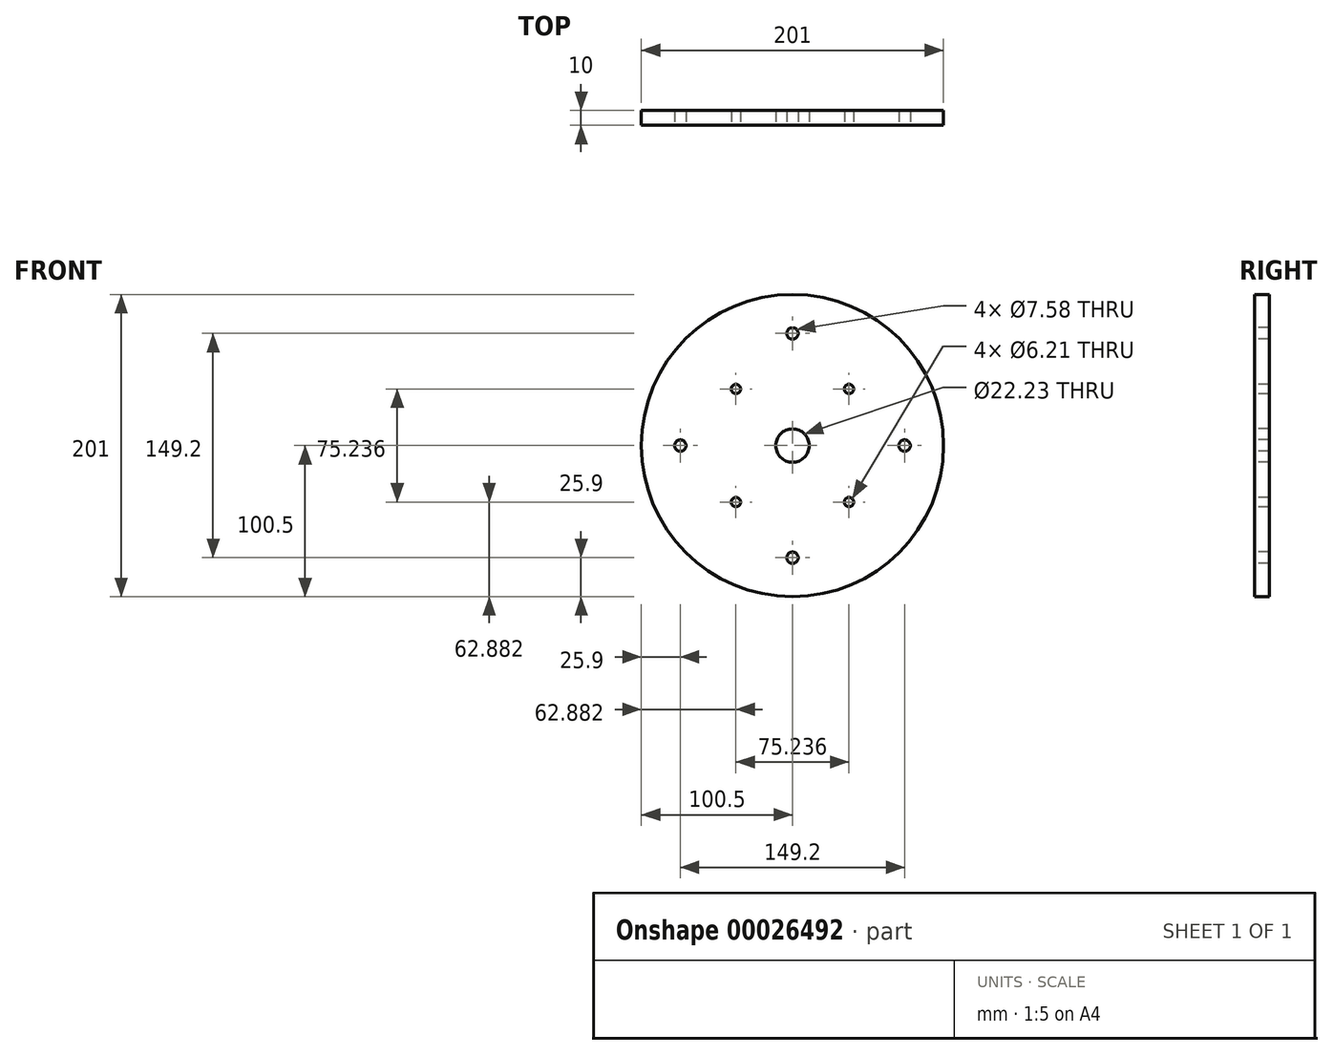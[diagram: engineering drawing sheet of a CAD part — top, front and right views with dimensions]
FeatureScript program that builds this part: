
annotation { "Feature Type Name" : "Feature", "Feature Type Description" : "" }
export const myFeature = defineFeature(function(context is Context, id is Id, definition is map)
    precondition{}
    {
        {
            var Q0;
            Q0=qCreatedBy(makeId("Front.planeOp"),FACE);
            var sketch = newSketch(context, id + "F0", { "sketchPlane" : qUnion([Q0])});
            skCircle(sketch, "E0", {"center": v(0, 0) * mm, "radius": 100.5 * mm});
            skCircle(sketch, "E1", {"center": v(0, 0) * mm, "radius": 53.2 * mm, "construction": true});
            skCircle(sketch, "E2", {"center": v(0, 0) * mm, "radius": 74.6 * mm, "construction": true});
            skLineSegment(sketch, "E3", {"start": v(0, 100.5) * mm, "end": v(0, -100.5) * mm, "construction": true});
            skLineSegment(sketch, "E4", {"start": v(-100.5, 0) * mm, "end": v(100.5, 0) * mm, "construction": true});
            skLineSegment(sketch, "E5", {"start": v(-71.06, -71.06) * mm, "end": v(71.06, 71.06) * mm, "construction": true});
            skLineSegment(sketch, "E6", {"start": v(-71.06, 71.06) * mm, "end": v(71.06, -71.06) * mm, "construction": true});
            skPoint(sketch, "E7", {"position": v(0, 74.6) * mm});
            skPoint(sketch, "E8", {"position": v(0, -74.6) * mm});
            skPoint(sketch, "E9", {"position": v(-74.6, 0) * mm});
            skPoint(sketch, "E10", {"position": v(74.6, 0) * mm});
            skPoint(sketch, "E11", {"position": v(-37.62, 37.62) * mm});
            skPoint(sketch, "E12", {"position": v(-37.62, -37.62) * mm});
            skPoint(sketch, "E13", {"position": v(37.62, -37.62) * mm});
            skPoint(sketch, "E14", {"position": v(37.62, 37.62) * mm});
            skCircle(sketch, "E15", {"center": v(0, 0) * mm, "radius": 11.11 * mm});
            skSolve(sketch);
        }
        {
            var Q0;
            Q0=makeQuery(id+"F0.imprint","IMPRINT",FACE,{"disambiguationData":[TD([[makeQuery(id+"F0.imprint","IMPRINT",EDGE,{"derivedFrom":sQuery(id+"F0.wireOp",EDGE,"E0")}),1.0]])]});
            extrude(context, id + "F1", {"entities" : qUnion([Q0]), "oppositeDirection" : true, "depth" : 10 * mm});
        }
        {
            var Q0;
            Q0=sQuery(id+"F0.wireOp",VERTEX,"E9");
            var Q1;
            Q1=sQuery(id+"F0.wireOp",VERTEX,"E7");
            var Q2;
            Q2=sQuery(id+"F0.wireOp",VERTEX,"E10");
            var Q3;
            Q3=sQuery(id+"F0.wireOp",VERTEX,"E8");
            var Q4;
            Q4=makeQuery(id+"F1.opExtrude","SWEPT_BODY",BODY,{"disambiguationData":[OSD([sQuery(id+"F0.wireOp",EDGE,"E0")])]});
            hole(context, id + "F2", {"style" : HoleStyle.SIMPLE, "holeDiameter" : 7.58 * mm, "endStyle" : HoleEndStyle.THROUGH, "locations" : qUnion([Q0, Q1, Q2, Q3]), "scope" : qUnion([Q4])});
        }
        {
            var Q0;
            Q0=sQuery(id+"F0.wireOp",VERTEX,"E11");
            var Q1;
            Q1=sQuery(id+"F0.wireOp",VERTEX,"E14");
            var Q2;
            Q2=sQuery(id+"F0.wireOp",VERTEX,"E13");
            var Q3;
            Q3=sQuery(id+"F0.wireOp",VERTEX,"E12");
            var Q4;
            Q4=makeQuery(id+"F1.opExtrude","SWEPT_BODY",BODY,{"disambiguationData":[OSD([sQuery(id+"F0.wireOp",EDGE,"E0")])]});
            hole(context, id + "F3", {"style" : HoleStyle.SIMPLE, "holeDiameter" : 6.2 * mm, "endStyle" : HoleEndStyle.THROUGH, "locations" : qUnion([Q0, Q1, Q2, Q3]), "scope" : qUnion([Q4])});
        }
    });
